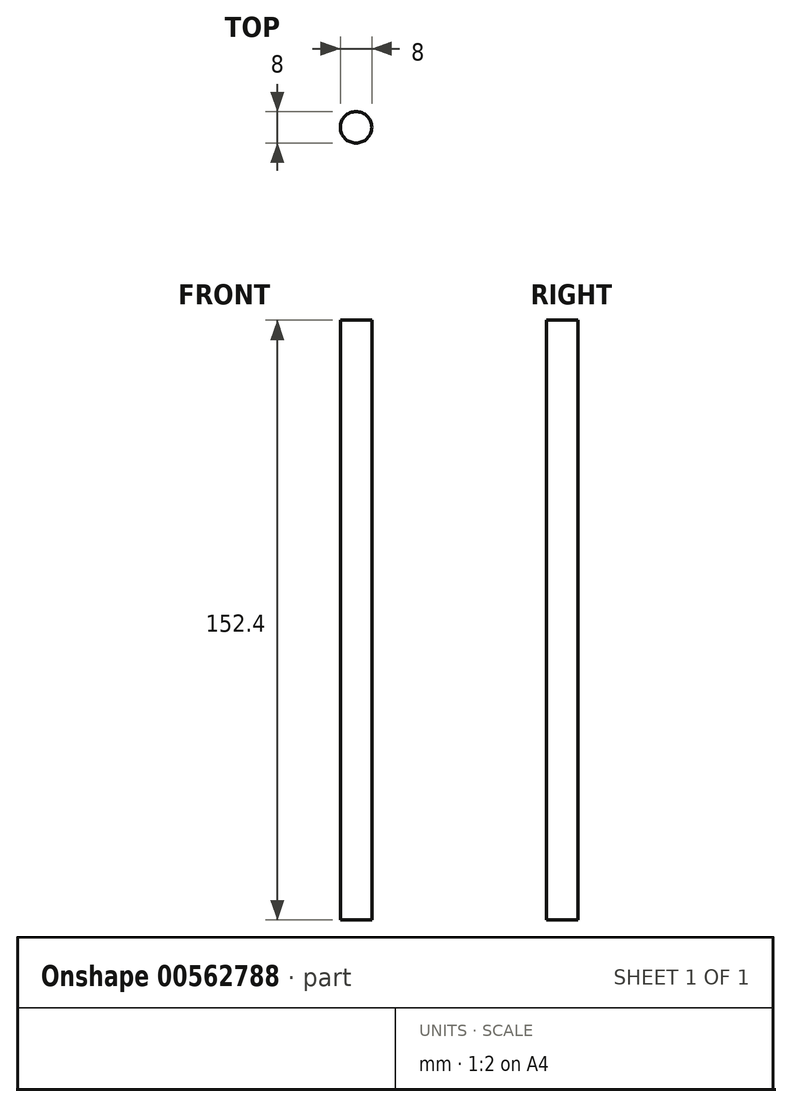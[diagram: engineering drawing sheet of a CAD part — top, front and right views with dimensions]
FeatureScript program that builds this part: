
annotation { "Feature Type Name" : "Feature", "Feature Type Description" : "" }
export const myFeature = defineFeature(function(context is Context, id is Id, definition is map)
    precondition{}
    {
        {
            var Q0;
            Q0=qCreatedBy(makeId("Top.planeOp"),FACE);
            var sketch = newSketch(context, id + "F0", { "sketchPlane" : qUnion([Q0])});
            skCircle(sketch, "E0", {"center": v(0, 0) * mm, "radius": 4 * mm});
            skSolve(sketch);
        }
        {
            var Q0;
            Q0 = qSketchRegion(id + "F0", true);
            extrude(context, id + "F1", {"entities" : qUnion([Q0]), "depth" : 152.4 * mm, "offsetDistance" : 25.4 * mm});
        }
    });
